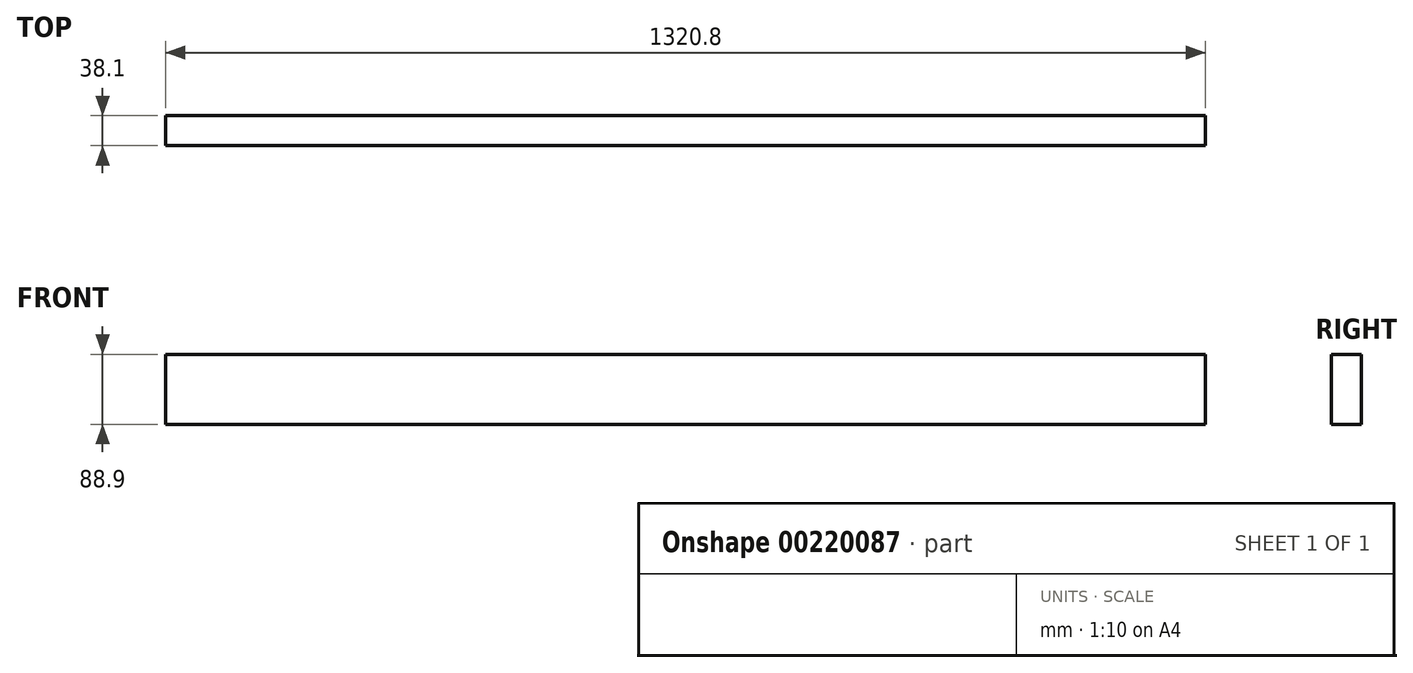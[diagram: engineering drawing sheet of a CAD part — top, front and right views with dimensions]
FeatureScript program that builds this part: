
annotation { "Feature Type Name" : "Feature", "Feature Type Description" : "" }
export const myFeature = defineFeature(function(context is Context, id is Id, definition is map)
    precondition{}
    {
        {
            var Q0;
            Q0=qCreatedBy(makeId("Right.planeOp"),FACE);
            var sketch = newSketch(context, id + "F0", { "sketchPlane" : qUnion([Q0])});
            skLineSegment(sketch, "E0.bottom", {"start": v(19.05, 44.45) * mm, "end": v(-19.05, 44.45) * mm});
            skLineSegment(sketch, "E0.top", {"start": v(19.05, -44.45) * mm, "end": v(-19.05, -44.45) * mm});
            skLineSegment(sketch, "E0.left", {"start": v(19.05, 44.45) * mm, "end": v(19.05, -44.45) * mm});
            skLineSegment(sketch, "E0.right", {"start": v(-19.05, 44.45) * mm, "end": v(-19.05, -44.45) * mm});
            skPoint(sketch, "E0.middle", {"position": v(0, 0) * mm});
            skSolve(sketch);
        }
        {
            var Q0;
            Q0 = qSketchRegion(id + "F0", true);
            extrude(context, id + "F1", {"entities" : qUnion([Q0]), "endBound" : BoundingType.SYMMETRIC, "depth" : 1320.8 * mm});
        }
    });
